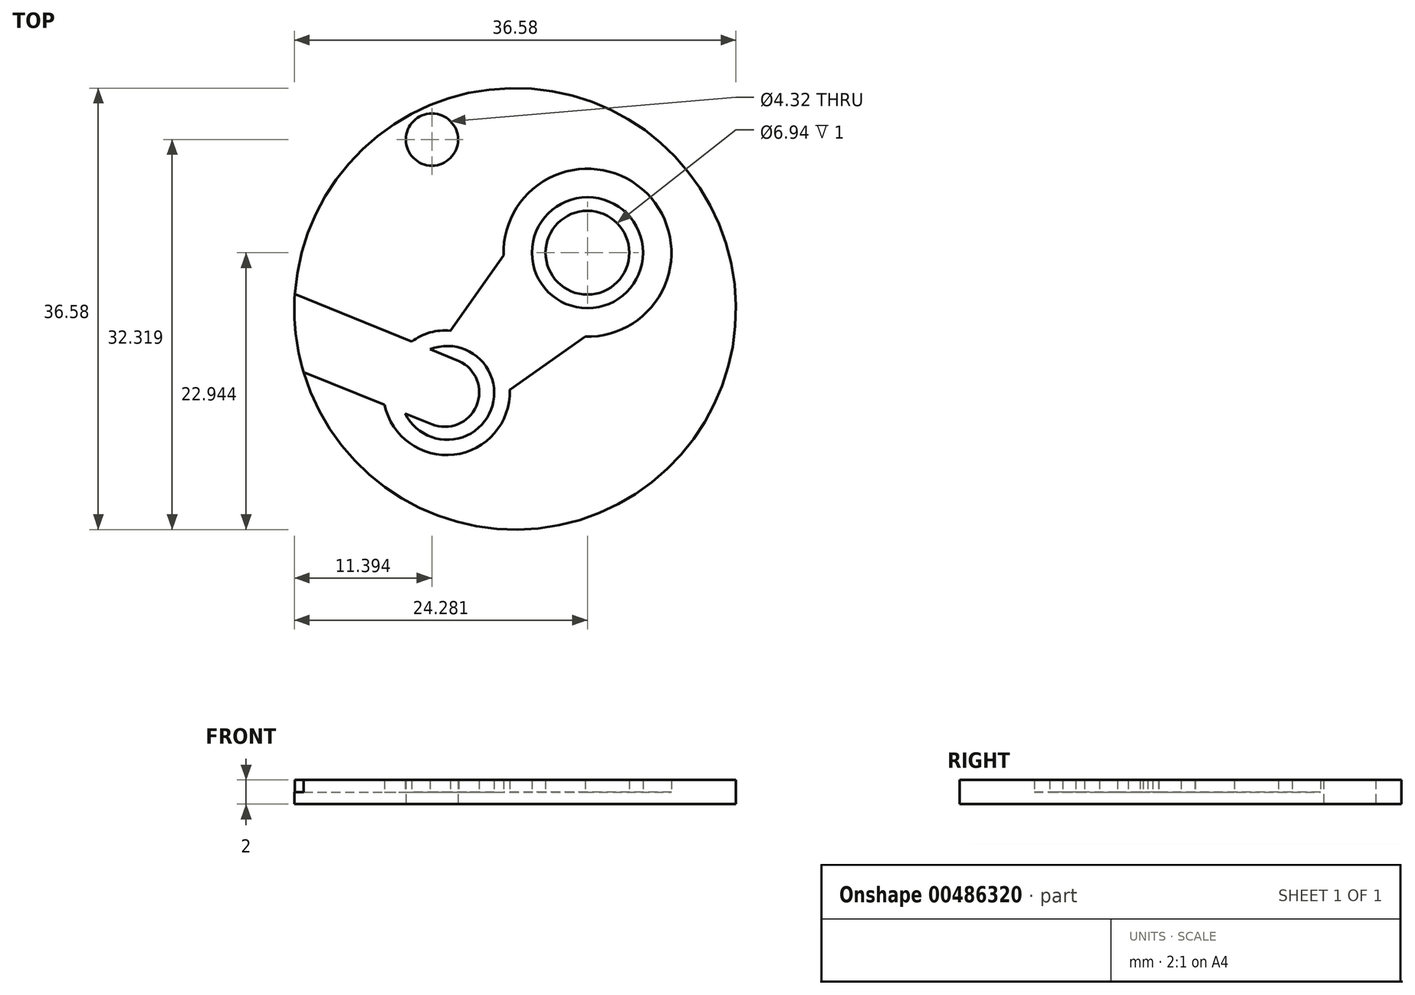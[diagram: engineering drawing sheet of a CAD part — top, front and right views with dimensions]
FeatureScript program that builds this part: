
annotation { "Feature Type Name" : "Feature", "Feature Type Description" : "" }
export const myFeature = defineFeature(function(context is Context, id is Id, definition is map)
    precondition{}
    {
        {
            var Q0;
            Q0=qCreatedBy(makeId("Top.planeOp"),FACE);
            var sketch = newSketch(context, id + "F0", { "sketchPlane" : qUnion([Q0])});
            skCircle(sketch, "E0", {"center": v(19.29, 20.15) * mm, "radius": 18.3 * mm});
            skPoint(sketch, "E0.first.point", {"position": v(20, 1.88) * mm});
            skPoint(sketch, "E0.first.point.positionSnap0", {"position": v(20, 0) * mm});
            skPoint(sketch, "E0.second.point", {"position": v(37.58, 20) * mm});
            skPoint(sketch, "E0.second.point.positionSnap0", {"position": v(40, 20) * mm});
            skPoint(sketch, "E0.third.point", {"position": v(1.04, 18.97) * mm});
            skLineSegment(sketch, "E1", {"start": v(1.04, 21.39) * mm, "end": v(10.73, 17.44) * mm});
            skLineSegment(sketch, "E2", {"start": v(1.76, 14.92) * mm, "end": v(8.48, 12.2) * mm});
            skArc(sketch, "E3", {"start": v(13.93, 18.34) * mm, "mid": v(12.24, 18.2) * mm, "end": v(10.73, 17.44) * mm});
            skArc(sketch, "E4", {"start": v(8.48, 12.2) * mm, "mid": v(14.22, 8.07) * mm, "end": v(18.85, 13.44) * mm});
            skLineSegment(sketch, "E5", {"start": v(18.85, 13.44) * mm, "end": v(25.09, 17.85) * mm});
            skLineSegment(sketch, "E6", {"start": v(13.93, 18.34) * mm, "end": v(18.33, 24.6) * mm});
            skArc(sketch, "E7", {"start": v(25.09, 17.85) * mm, "mid": v(30.2, 29.73) * mm, "end": v(18.33, 24.6) * mm});
            skCircle(sketch, "E8", {"center": v(25.28, 24.8) * mm, "radius": 3.47 * mm});
            skCircle(sketch, "E9", {"center": v(25.28, 24.8) * mm, "radius": 4.6 * mm});
            skLineSegment(sketch, "E10", {"start": v(10.18, 11.48) * mm, "end": v(12.39, 10.59) * mm});
            skLineSegment(sketch, "E11", {"start": v(12.24, 16.8) * mm, "end": v(14.63, 15.83) * mm});
            skArc(sketch, "E12", {"start": v(12.39, 10.59) * mm, "mid": v(16.08, 12.11) * mm, "end": v(14.63, 15.83) * mm});
            skArc(sketch, "E13", {"start": v(10.18, 11.48) * mm, "mid": v(17.3, 11.79) * mm, "end": v(12.24, 16.8) * mm});
            skCircle(sketch, "E14", {"center": v(12.4, 34.18) * mm, "radius": 2.16 * mm});
            skSolve(sketch);
        }
        {
            var Q0;
            {var subQ1=sQuery(id+"F0.wireOp",EDGE,"E1");Q0=makeQuery(id+"F0.imprint","IMPRINT",FACE,{"disambiguationData":[TD([[makeQuery(id+"F0.imprint","IMPRINT",EDGE,{"derivedFrom":subQ1}),1.0]])]});}
            extrude(context, id + "F1", {"entities" : qUnion([Q0]), "depth" : 2 * mm, "offsetDistance" : 25 * mm});
        }
        {
            var Q0;
            {var subQ1=sQuery(id+"F0.wireOp",EDGE,"E1");Q0=makeQuery(id+"F0.imprint","IMPRINT",FACE,{"disambiguationData":[TD([[makeQuery(id+"F0.imprint","IMPRINT",EDGE,{"derivedFrom":subQ1}),-1.0]])]});}
            var Q1;
            Q1=makeQuery(id+"F0.imprint","IMPRINT",FACE,{"disambiguationData":[TD([[makeQuery(id+"F0.imprint","IMPRINT",EDGE,{"derivedFrom":sQuery(id+"F0.wireOp",EDGE,"E8")}),1.0]])]});
            extrude(context, id + "F2", {"entities" : qUnion([Q0, Q1]), "operationType" : NewBodyOperationType.ADD, "depth" : 1 * mm, "offsetDistance" : 25 * mm});
        }
        {
            var Q0;
            Q0=makeQuery(id+"F0.imprint","IMPRINT",FACE,{"disambiguationData":[TD([[makeQuery(id+"F0.imprint","IMPRINT",EDGE,{"derivedFrom":sQuery(id+"F0.wireOp",EDGE,"E10")}),-1.0]])]});
            var Q1;
            Q1=makeQuery(id+"F0.imprint","IMPRINT",FACE,{"disambiguationData":[TD([[makeQuery(id+"F0.imprint","IMPRINT",EDGE,{"derivedFrom":sQuery(id+"F0.wireOp",EDGE,"E8")}),-1.0]])]});
            extrude(context, id + "F3", {"entities" : qUnion([Q0, Q1]), "operationType" : NewBodyOperationType.ADD, "depth" : 2 * mm, "offsetDistance" : 25 * mm});
        }
    });
